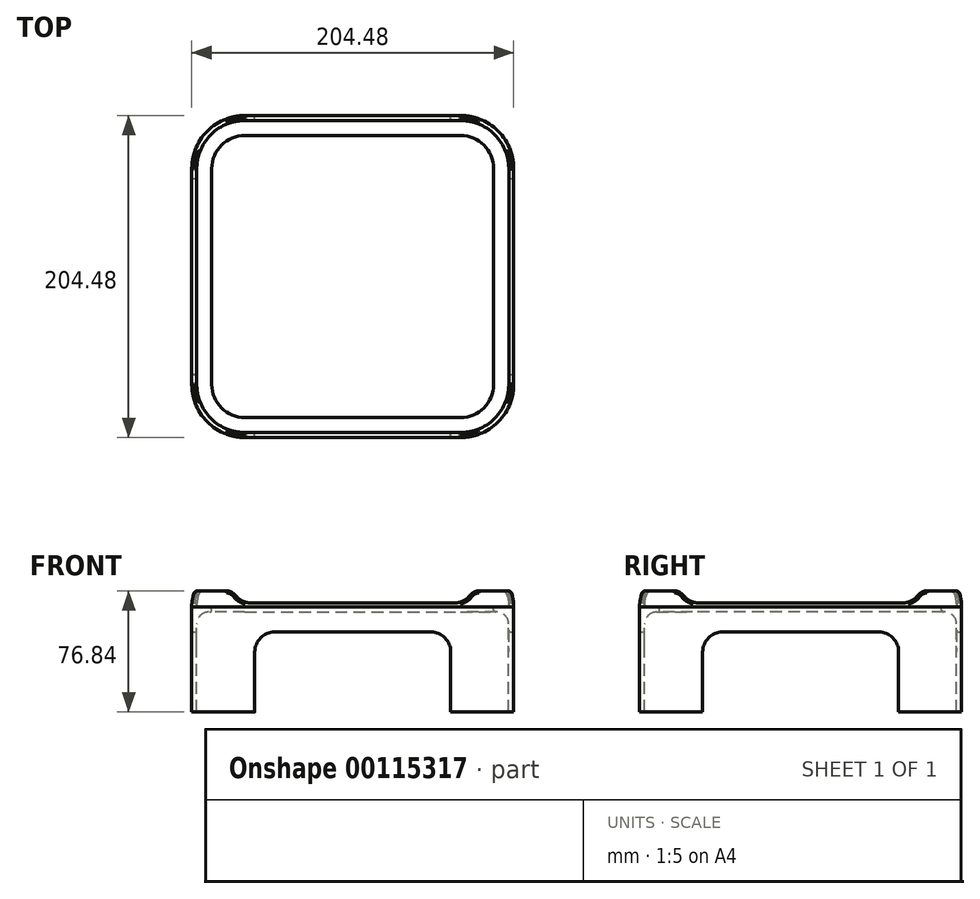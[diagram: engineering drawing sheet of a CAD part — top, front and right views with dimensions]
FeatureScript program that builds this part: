
annotation { "Feature Type Name" : "Feature", "Feature Type Description" : "" }
export const myFeature = defineFeature(function(context is Context, id is Id, definition is map)
    precondition{}
    {
        {
            var Q0;
            Q0=qCreatedBy(makeId("Top.planeOp"),FACE);
            var sketch = newSketch(context, id + "F0", { "sketchPlane" : qUnion([Q0])});
            skLineSegment(sketch, "E0.bottom", {"start": v(-99.06, 99.06) * mm, "end": v(99.06, 99.06) * mm});
            skLineSegment(sketch, "E0.top", {"start": v(-99.06, -99.06) * mm, "end": v(99.06, -99.06) * mm});
            skLineSegment(sketch, "E0.left", {"start": v(-99.06, 99.06) * mm, "end": v(-99.06, -99.06) * mm});
            skLineSegment(sketch, "E0.right", {"start": v(99.06, 99.06) * mm, "end": v(99.06, -99.06) * mm});
            skPoint(sketch, "E0.middle", {"position": v(0, 0) * mm});
            skSolve(sketch);
        }
        {
            var Q0;
            Q0=makeQuery(id+"F0.imprint","IMPRINT",FACE,{"disambiguationData":[TD([[makeQuery(id+"F0.imprint","IMPRINT",EDGE,{"derivedFrom":sQuery(id+"F0.wireOp",EDGE,"E0.bottom")}),-1.0]])]});
            extrude(context, id + "F1", {"entities" : qUnion([Q0]), "oppositeDirection" : true, "depth" : 63.5 * mm});
        }
        {
            var Q0;
            Q0=makeQuery(id+"F1.opExtrude","SWEPT_EDGE",EDGE,{"disambiguationData":[OSD([sQuery(id+"F0.wireOp",EDGE,"E0.top"),sQuery(id+"F0.wireOp",EDGE,"E0.right")])]});
            var Q1;
            Q1=makeQuery(id+"F1.opExtrude","SWEPT_EDGE",EDGE,{"disambiguationData":[OSD([sQuery(id+"F0.wireOp",EDGE,"E0.top"),sQuery(id+"F0.wireOp",EDGE,"E0.left")])]});
            var Q2;
            Q2=makeQuery(id+"F1.opExtrude","SWEPT_EDGE",EDGE,{"disambiguationData":[OSD([sQuery(id+"F0.wireOp",EDGE,"E0.bottom"),sQuery(id+"F0.wireOp",EDGE,"E0.right")])]});
            var Q3;
            Q3=makeQuery(id+"F1.opExtrude","SWEPT_EDGE",EDGE,{"disambiguationData":[OSD([sQuery(id+"F0.wireOp",EDGE,"E0.bottom"),sQuery(id+"F0.wireOp",EDGE,"E0.left")])]});
            fillet(context, id + "F2", {"entities" : qUnion([Q0, Q1, Q2, Q3]), "radius" : 30.48 * mm, "tangentPropagation" : true, "allowEdgeOverflow" : false});
        }
        {
            var Q0;
            Q0=makeQuery(id+"F1.opExtrude","CAP_FACE",FACE,{"disambiguationData":[OSD([sQuery(id+"F0.wireOp",EDGE,"E0.bottom"),sQuery(id+"F0.wireOp",EDGE,"E0.top"),sQuery(id+"F0.wireOp",EDGE,"E0.left"),sQuery(id+"F0.wireOp",EDGE,"E0.right")])],"isStart":false});
            shell(context, id + "F3", {"entities" : qUnion([Q0]), "thickness" : 3.17 * mm, "oppositeDirection" : true});
        }
        {
            var Q0;
            Q0=makeQuery(id+"F1.opExtrude","SWEPT_FACE",FACE,{"disambiguationData":[OSD([sQuery(id+"F0.wireOp",EDGE,"E0.bottom")])]});
            var sketch = newSketch(context, id + "F4", { "sketchPlane" : qUnion([Q0])});
            skLineSegment(sketch, "E1.bottom", {"start": v(-62.23, -12.7) * mm, "end": v(62.23, -12.7) * mm});
            skLineSegment(sketch, "E1.top", {"start": v(-62.23, -63.5) * mm, "end": v(62.23, -63.5) * mm});
            skLineSegment(sketch, "E1.left", {"start": v(-62.23, -12.7) * mm, "end": v(-62.23, -63.5) * mm});
            skLineSegment(sketch, "E1.right", {"start": v(62.23, -12.7) * mm, "end": v(62.23, -63.5) * mm});
            skSolve(sketch);
        }
        {
            var Q0;
            Q0=makeQuery(id+"F1.opExtrude","SWEPT_FACE",FACE,{"disambiguationData":[OSD([sQuery(id+"F0.wireOp",EDGE,"E0.right")])]});
            var sketch = newSketch(context, id + "F5", { "sketchPlane" : qUnion([Q0])});
            skLineSegment(sketch, "E2.bottom", {"start": v(-62.23, -12.7) * mm, "end": v(62.23, -12.7) * mm});
            skLineSegment(sketch, "E2.top", {"start": v(-62.23, -63.5) * mm, "end": v(62.23, -63.5) * mm});
            skLineSegment(sketch, "E2.left", {"start": v(-62.23, -12.7) * mm, "end": v(-62.23, -63.5) * mm});
            skLineSegment(sketch, "E2.right", {"start": v(62.23, -12.7) * mm, "end": v(62.23, -63.5) * mm});
            skSolve(sketch);
        }
        {
            var Q0;
            Q0=makeQuery(id+"F4.imprint","IMPRINT",FACE,{"disambiguationData":[TD([[makeQuery(id+"F4.imprint","IMPRINT",EDGE,{"derivedFrom":sQuery(id+"F4.wireOp",EDGE,"E1.bottom")}),-1.0]])]});
            extrude(context, id + "F6", {"entities" : qUnion([Q0]), "operationType" : NewBodyOperationType.REMOVE, "endBound" : BoundingType.THROUGH_ALL, "oppositeDirection" : true, "depth" : 25.4 * mm});
        }
        {
            var Q0;
            Q0=makeQuery(id+"F5.imprint","IMPRINT",FACE,{"disambiguationData":[TD([[makeQuery(id+"F5.imprint","IMPRINT",EDGE,{"derivedFrom":sQuery(id+"F5.wireOp",EDGE,"E2.bottom")}),-1.0]])]});
            extrude(context, id + "F7", {"entities" : qUnion([Q0]), "operationType" : NewBodyOperationType.REMOVE, "endBound" : BoundingType.THROUGH_ALL, "oppositeDirection" : true, "depth" : 25.4 * mm});
        }
        {
            var Q0;
            Q0=makeQuery(id+"F6.boolean.opBoolean","COPY",EDGE,{"disambiguationData":[OD(0.0)],"derivedFrom":makeQuery(id+"F6.opExtrude","SWEPT_EDGE",EDGE,{"disambiguationData":[OSD([sQuery(id+"F4.wireOp",EDGE,"E1.bottom"),sQuery(id+"F4.wireOp",EDGE,"E1.left")])]})});
            var Q1;
            Q1=makeQuery(id+"F6.boolean.opBoolean","COPY",EDGE,{"disambiguationData":[OD(0.0)],"derivedFrom":makeQuery(id+"F6.opExtrude","SWEPT_EDGE",EDGE,{"disambiguationData":[OSD([sQuery(id+"F4.wireOp",EDGE,"E1.bottom"),sQuery(id+"F4.wireOp",EDGE,"E1.right")])]})});
            var Q2;
            Q2=makeQuery(id+"F7.boolean.opBoolean","COPY",EDGE,{"disambiguationData":[OD(1.0)],"derivedFrom":makeQuery(id+"F7.opExtrude","SWEPT_EDGE",EDGE,{"disambiguationData":[OSD([sQuery(id+"F5.wireOp",EDGE,"E2.bottom"),sQuery(id+"F5.wireOp",EDGE,"E2.right")])]})});
            var Q3;
            Q3=makeQuery(id+"F7.boolean.opBoolean","COPY",EDGE,{"disambiguationData":[OD(1.0)],"derivedFrom":makeQuery(id+"F7.opExtrude","SWEPT_EDGE",EDGE,{"disambiguationData":[OSD([sQuery(id+"F5.wireOp",EDGE,"E2.bottom"),sQuery(id+"F5.wireOp",EDGE,"E2.left")])]})});
            var Q4;
            Q4=makeQuery(id+"F6.boolean.opBoolean","COPY",EDGE,{"disambiguationData":[OD(1.0)],"derivedFrom":makeQuery(id+"F6.opExtrude","SWEPT_EDGE",EDGE,{"disambiguationData":[OSD([sQuery(id+"F4.wireOp",EDGE,"E1.bottom"),sQuery(id+"F4.wireOp",EDGE,"E1.right")])]})});
            var Q5;
            Q5=makeQuery(id+"F7.boolean.opBoolean","COPY",EDGE,{"disambiguationData":[OD(0.0)],"derivedFrom":makeQuery(id+"F7.opExtrude","SWEPT_EDGE",EDGE,{"disambiguationData":[OSD([sQuery(id+"F5.wireOp",EDGE,"E2.bottom"),sQuery(id+"F5.wireOp",EDGE,"E2.right")])]})});
            var Q6;
            Q6=makeQuery(id+"F6.boolean.opBoolean","COPY",EDGE,{"disambiguationData":[OD(1.0)],"derivedFrom":makeQuery(id+"F6.opExtrude","SWEPT_EDGE",EDGE,{"disambiguationData":[OSD([sQuery(id+"F4.wireOp",EDGE,"E1.bottom"),sQuery(id+"F4.wireOp",EDGE,"E1.left")])]})});
            var Q7;
            Q7=makeQuery(id+"F7.boolean.opBoolean","COPY",EDGE,{"disambiguationData":[OD(0.0)],"derivedFrom":makeQuery(id+"F7.opExtrude","SWEPT_EDGE",EDGE,{"disambiguationData":[OSD([sQuery(id+"F5.wireOp",EDGE,"E2.bottom"),sQuery(id+"F5.wireOp",EDGE,"E2.left")])]})});
            fillet(context, id + "F8", {"entities" : qUnion([Q0, Q1, Q2, Q3, Q4, Q5, Q6, Q7]), "radius" : 12.7 * mm, "tangentPropagation" : true, "allowEdgeOverflow" : false});
        }
        {
            var Q0;
            Q0=makeQuery(id+"F1.opExtrude","CAP_FACE",FACE,{"disambiguationData":[OSD([sQuery(id+"F0.wireOp",EDGE,"E0.bottom"),sQuery(id+"F0.wireOp",EDGE,"E0.top"),sQuery(id+"F0.wireOp",EDGE,"E0.left"),sQuery(id+"F0.wireOp",EDGE,"E0.right")])],"isStart":true});
            extrude(context, id + "F9", {"entities" : qUnion([Q0]), "depth" : 10.16 * mm});
        }
        {
            var Q0;
            Q0=makeQuery(id+"F9.opExtrude","CAP_FACE",FACE,{"disambiguationData":[OSD([sQuery(id+"F0.wireOp",EDGE,"E0.bottom"),sQuery(id+"F0.wireOp",EDGE,"E0.top"),sQuery(id+"F0.wireOp",EDGE,"E0.left"),sQuery(id+"F0.wireOp",EDGE,"E0.right")])],"isStart":false});
            var Q1;
            Q1=makeQuery(id+"F9.opExtrude","CAP_FACE",FACE,{"disambiguationData":[OSD([sQuery(id+"F0.wireOp",EDGE,"E0.bottom"),sQuery(id+"F0.wireOp",EDGE,"E0.top"),sQuery(id+"F0.wireOp",EDGE,"E0.left"),sQuery(id+"F0.wireOp",EDGE,"E0.right")])],"isStart":true});
            shell(context, id + "F10", {"entities" : qUnion([Q0, Q1]), "thickness" : 3.15 * mm});
        }
        {
            var Q0;
            Q0=makeQuery(id+"F9.opExtrude","CAP_FACE",FACE,{"disambiguationData":[OSD([sQuery(id+"F0.wireOp",EDGE,"E0.bottom"),sQuery(id+"F0.wireOp",EDGE,"E0.top"),sQuery(id+"F0.wireOp",EDGE,"E0.left"),sQuery(id+"F0.wireOp",EDGE,"E0.right")])],"isStart":false});
            var sketch = newSketch(context, id + "F11", { "sketchPlane" : qUnion([Q0])});
            skLineSegment(sketch, "E3.bottom", {"start": v(-114.3, 76.2) * mm, "end": v(114.3, 76.2) * mm});
            skLineSegment(sketch, "E3.top", {"start": v(-114.3, -76.2) * mm, "end": v(114.3, -76.2) * mm});
            skLineSegment(sketch, "E3.left", {"start": v(-114.3, 76.2) * mm, "end": v(-114.3, -76.2) * mm});
            skLineSegment(sketch, "E3.right", {"start": v(114.3, 76.2) * mm, "end": v(114.3, -76.2) * mm});
            skPoint(sketch, "E3.middle", {"position": v(0, 0) * mm});
            skLineSegment(sketch, "E4.bottom", {"start": v(-76.2, 114.3) * mm, "end": v(76.2, 114.3) * mm});
            skLineSegment(sketch, "E4.top", {"start": v(-76.2, -114.3) * mm, "end": v(76.2, -114.3) * mm});
            skLineSegment(sketch, "E4.left", {"start": v(-76.2, 114.3) * mm, "end": v(-76.2, -114.3) * mm});
            skLineSegment(sketch, "E4.right", {"start": v(76.2, 114.3) * mm, "end": v(76.2, -114.3) * mm});
            skSolve(sketch);
        }
        {
            var Q0;
            {var subQ0=sQuery(id+"F11.wireOp",EDGE,"E3.right");Q0=makeQuery(id+"F11.imprint","IMPRINT",FACE,{"disambiguationData":[TD([[makeQuery(id+"F11.imprint","IMPRINT",EDGE,{"derivedFrom":subQ0}),-1.0]])]});}
            var Q1;
            {var subQ0=sQuery(id+"F11.wireOp",EDGE,"E4.right");var subQ1=sQuery(id+"F11.wireOp",EDGE,"E3.bottom");var subQ2=makeQuery(id+"F11.imprint","INTERSECT",VERTEX,{"derivedFrom":[subQ1,subQ0]});Q1=makeQuery(id+"F11.imprint","IMPRINT",FACE,{"disambiguationData":[TD([[makeQuery(id+"F11.imprint","IMPRINT",EDGE,{"disambiguationData":[TD([[subQ2,-1.0]])],"derivedFrom":subQ0}),1.0]])]});}
            var Q2;
            {var subQ0=sQuery(id+"F11.wireOp",EDGE,"E3.bottom");var subQ1=sQuery(id+"F0.wireOp",EDGE,"E0.right");var subQ2=makeQuery(id+"F9.opExtrude","CAP_EDGE",EDGE,{"disambiguationData":[OSD([subQ1])],"isStart":false});var subQ3=makeQuery(id+"F11.imprint","INTERSECT",VERTEX,{"derivedFrom":[subQ2,subQ0]});Q2=makeQuery(id+"F11.imprint","IMPRINT",FACE,{"disambiguationData":[TD([[makeQuery(id+"F11.imprint","IMPRINT",EDGE,{"disambiguationData":[TD([[subQ3,-1.0]])],"derivedFrom":subQ2}),-1.0]])]});}
            var Q3;
            {var subQ0=sQuery(id+"F11.wireOp",EDGE,"E4.left");var subQ1=sQuery(id+"F11.wireOp",EDGE,"E3.top");var subQ2=makeQuery(id+"F11.imprint","INTERSECT",VERTEX,{"derivedFrom":[subQ1,subQ0]});Q3=makeQuery(id+"F11.imprint","IMPRINT",FACE,{"disambiguationData":[TD([[makeQuery(id+"F11.imprint","IMPRINT",EDGE,{"disambiguationData":[TD([[subQ2,-1.0]])],"derivedFrom":subQ1}),-1.0]])]});}
            var Q4;
            {var subQ0=sQuery(id+"F11.wireOp",EDGE,"E4.left");var subQ1=sQuery(id+"F0.wireOp",EDGE,"E0.top");var subQ2=makeQuery(id+"F9.opExtrude","CAP_EDGE",EDGE,{"disambiguationData":[OSD([subQ1])],"isStart":false});var subQ3=makeQuery(id+"F11.imprint","INTERSECT",VERTEX,{"derivedFrom":[subQ2,subQ0]});Q4=makeQuery(id+"F11.imprint","IMPRINT",FACE,{"disambiguationData":[TD([[makeQuery(id+"F11.imprint","IMPRINT",EDGE,{"disambiguationData":[TD([[subQ3,-1.0]])],"derivedFrom":subQ2}),1.0]])]});}
            var Q5;
            {var subQ0=sQuery(id+"F11.wireOp",EDGE,"E4.top");Q5=makeQuery(id+"F11.imprint","IMPRINT",FACE,{"disambiguationData":[TD([[makeQuery(id+"F11.imprint","IMPRINT",EDGE,{"derivedFrom":subQ0}),1.0]])]});}
            var Q6;
            {var subQ0=sQuery(id+"F11.wireOp",EDGE,"E4.bottom");Q6=makeQuery(id+"F11.imprint","IMPRINT",FACE,{"disambiguationData":[TD([[makeQuery(id+"F11.imprint","IMPRINT",EDGE,{"derivedFrom":subQ0}),-1.0]])]});}
            var Q7;
            {var subQ0=sQuery(id+"F11.wireOp",EDGE,"E4.left");var subQ1=sQuery(id+"F11.wireOp",EDGE,"E3.bottom");var subQ2=makeQuery(id+"F11.imprint","INTERSECT",VERTEX,{"derivedFrom":[subQ1,subQ0]});Q7=makeQuery(id+"F11.imprint","IMPRINT",FACE,{"disambiguationData":[TD([[makeQuery(id+"F11.imprint","IMPRINT",EDGE,{"disambiguationData":[TD([[subQ2,-1.0]])],"derivedFrom":subQ1}),1.0]])]});}
            var Q8;
            {var subQ0=sQuery(id+"F11.wireOp",EDGE,"E4.left");var subQ1=sQuery(id+"F0.wireOp",EDGE,"E0.bottom");var subQ2=makeQuery(id+"F9.opExtrude","CAP_EDGE",EDGE,{"disambiguationData":[OSD([subQ1])],"isStart":false});var subQ3=makeQuery(id+"F11.imprint","INTERSECT",VERTEX,{"derivedFrom":[subQ2,subQ0]});Q8=makeQuery(id+"F11.imprint","IMPRINT",FACE,{"disambiguationData":[TD([[makeQuery(id+"F11.imprint","IMPRINT",EDGE,{"disambiguationData":[TD([[subQ3,-1.0]])],"derivedFrom":subQ2}),-1.0]])]});}
            var Q9;
            {var subQ0=sQuery(id+"F11.wireOp",EDGE,"E3.left");Q9=makeQuery(id+"F11.imprint","IMPRINT",FACE,{"disambiguationData":[TD([[makeQuery(id+"F11.imprint","IMPRINT",EDGE,{"derivedFrom":subQ0}),1.0]])]});}
            var Q10;
            {var subQ0=sQuery(id+"F11.wireOp",EDGE,"E3.bottom");var subQ1=sQuery(id+"F0.wireOp",EDGE,"E0.left");var subQ2=makeQuery(id+"F9.opExtrude","CAP_EDGE",EDGE,{"disambiguationData":[OSD([subQ1])],"isStart":false});var subQ3=makeQuery(id+"F11.imprint","INTERSECT",VERTEX,{"derivedFrom":[subQ2,subQ0]});Q10=makeQuery(id+"F11.imprint","IMPRINT",FACE,{"disambiguationData":[TD([[makeQuery(id+"F11.imprint","IMPRINT",EDGE,{"disambiguationData":[TD([[subQ3,-1.0]])],"derivedFrom":subQ2}),1.0]])]});}
            var Q11;
            {var subQ0=sQuery(id+"F11.wireOp",EDGE,"E4.left");var subQ1=sQuery(id+"F11.wireOp",EDGE,"E3.bottom");var subQ2=makeQuery(id+"F11.imprint","INTERSECT",VERTEX,{"derivedFrom":[subQ1,subQ0]});Q11=makeQuery(id+"F11.imprint","IMPRINT",FACE,{"disambiguationData":[TD([[makeQuery(id+"F11.imprint","IMPRINT",EDGE,{"disambiguationData":[TD([[subQ2,-1.0]])],"derivedFrom":subQ0}),-1.0]])]});}
            var Q12;
            {var subQ0=sQuery(id+"F11.wireOp",EDGE,"E4.left");var subQ1=sQuery(id+"F11.wireOp",EDGE,"E3.bottom");var subQ2=makeQuery(id+"F11.imprint","INTERSECT",VERTEX,{"derivedFrom":[subQ1,subQ0]});Q12=makeQuery(id+"F11.imprint","IMPRINT",FACE,{"disambiguationData":[TD([[makeQuery(id+"F11.imprint","IMPRINT",EDGE,{"disambiguationData":[TD([[subQ2,-1.0]])],"derivedFrom":subQ1}),-1.0]])]});}
            extrude(context, id + "F12", {"entities" : qUnion([Q0, Q1, Q2, Q3, Q4, Q5, Q6, Q7, Q8, Q9, Q10, Q11, Q12]), "operationType" : NewBodyOperationType.REMOVE, "oppositeDirection" : true, "depth" : 7.62 * mm});
        }
        {
            var Q0;
            {var subQ0=sQuery(id+"F11.wireOp",EDGE,"E3.bottom");var subQ1=sQuery(id+"F0.wireOp",EDGE,"E0.left");var subQ2=makeQuery(id+"F9.opExtrude","CAP_EDGE",EDGE,{"disambiguationData":[OSD([subQ1])],"isStart":false});var subQ4=makeQuery(id+"F11.imprint","INTERSECT",VERTEX,{"derivedFrom":[subQ2,subQ0]});Q0=makeQuery(id+"F12.boolean.opBoolean","COPY",EDGE,{"derivedFrom":makeQuery(id+"F12.opExtrude","CAP_EDGE",EDGE,{"disambiguationData":[OSD([subQ0]),TDD([makeQuery(id+"F11.imprint","IMPRINT",EDGE,{"disambiguationData":[TD([[makeQuery(id+"F11.imprint","INTERSECT",VERTEX,{"derivedFrom":[subQ0,sQuery(id+"F11.wireOp",EDGE,"E3.left")]}),-1.0]])],"derivedFrom":subQ0}),makeQuery(id+"F11.imprint","IMPRINT",EDGE,{"disambiguationData":[TD([[subQ4,-1.0]])],"derivedFrom":subQ0}),makeQuery(id+"F11.imprint","IMPRINT",EDGE,{"disambiguationData":[TD([[makeQuery(id+"F11.imprint","INTERSECT",VERTEX,{"derivedFrom":[subQ0,sQuery(id+"F11.wireOp",EDGE,"E4.left")]}),1.0]])],"derivedFrom":subQ0})])],"isStart":false})});}
            var Q1;
            {var subQ0=sQuery(id+"F11.wireOp",EDGE,"E3.top");var subQ1=sQuery(id+"F0.wireOp",EDGE,"E0.left");var subQ2=makeQuery(id+"F9.opExtrude","CAP_EDGE",EDGE,{"disambiguationData":[OSD([subQ1])],"isStart":false});var subQ4=makeQuery(id+"F11.imprint","INTERSECT",VERTEX,{"derivedFrom":[subQ2,subQ0]});Q1=makeQuery(id+"F12.boolean.opBoolean","COPY",EDGE,{"derivedFrom":makeQuery(id+"F12.opExtrude","CAP_EDGE",EDGE,{"disambiguationData":[OSD([subQ0]),TDD([makeQuery(id+"F11.imprint","IMPRINT",EDGE,{"disambiguationData":[TD([[makeQuery(id+"F11.imprint","INTERSECT",VERTEX,{"derivedFrom":[subQ0,sQuery(id+"F11.wireOp",EDGE,"E3.left")]}),-1.0]])],"derivedFrom":subQ0}),makeQuery(id+"F11.imprint","IMPRINT",EDGE,{"disambiguationData":[TD([[subQ4,-1.0]])],"derivedFrom":subQ0}),makeQuery(id+"F11.imprint","IMPRINT",EDGE,{"disambiguationData":[TD([[makeQuery(id+"F11.imprint","INTERSECT",VERTEX,{"derivedFrom":[subQ0,sQuery(id+"F11.wireOp",EDGE,"E4.left")]}),1.0]])],"derivedFrom":subQ0})])],"isStart":false})});}
            var Q2;
            {var subQ0=sQuery(id+"F11.wireOp",EDGE,"E4.left");var subQ1=sQuery(id+"F0.wireOp",EDGE,"E0.top");var subQ2=makeQuery(id+"F9.opExtrude","CAP_EDGE",EDGE,{"disambiguationData":[OSD([subQ1])],"isStart":false});var subQ3=makeQuery(id+"F11.imprint","INTERSECT",VERTEX,{"derivedFrom":[subQ2,subQ0]});Q2=makeQuery(id+"F12.boolean.opBoolean","COPY",EDGE,{"derivedFrom":makeQuery(id+"F12.opExtrude","CAP_EDGE",EDGE,{"disambiguationData":[OSD([subQ0]),TDD([makeQuery(id+"F11.imprint","IMPRINT",EDGE,{"disambiguationData":[TD([[makeQuery(id+"F11.imprint","INTERSECT",VERTEX,{"derivedFrom":[sQuery(id+"F11.wireOp",EDGE,"E3.top"),subQ0]}),-1.0]])],"derivedFrom":subQ0}),makeQuery(id+"F11.imprint","IMPRINT",EDGE,{"disambiguationData":[TD([[subQ3,1.0]])],"derivedFrom":subQ0}),makeQuery(id+"F11.imprint","IMPRINT",EDGE,{"disambiguationData":[TD([[makeQuery(id+"F11.imprint","INTERSECT",VERTEX,{"derivedFrom":[sQuery(id+"F11.wireOp",EDGE,"E4.top"),subQ0]}),1.0]])],"derivedFrom":subQ0})])],"isStart":false})});}
            var Q3;
            {var subQ0=sQuery(id+"F11.wireOp",EDGE,"E4.right");var subQ1=sQuery(id+"F0.wireOp",EDGE,"E0.top");var subQ2=makeQuery(id+"F9.opExtrude","CAP_EDGE",EDGE,{"disambiguationData":[OSD([subQ1])],"isStart":false});var subQ3=makeQuery(id+"F11.imprint","INTERSECT",VERTEX,{"derivedFrom":[subQ2,subQ0]});Q3=makeQuery(id+"F12.boolean.opBoolean","COPY",EDGE,{"derivedFrom":makeQuery(id+"F12.opExtrude","CAP_EDGE",EDGE,{"disambiguationData":[OSD([subQ0]),TDD([makeQuery(id+"F11.imprint","IMPRINT",EDGE,{"disambiguationData":[TD([[makeQuery(id+"F11.imprint","INTERSECT",VERTEX,{"derivedFrom":[sQuery(id+"F11.wireOp",EDGE,"E3.top"),subQ0]}),-1.0]])],"derivedFrom":subQ0}),makeQuery(id+"F11.imprint","IMPRINT",EDGE,{"disambiguationData":[TD([[subQ3,1.0]])],"derivedFrom":subQ0}),makeQuery(id+"F11.imprint","IMPRINT",EDGE,{"disambiguationData":[TD([[makeQuery(id+"F11.imprint","INTERSECT",VERTEX,{"derivedFrom":[sQuery(id+"F11.wireOp",EDGE,"E4.top"),subQ0]}),1.0]])],"derivedFrom":subQ0})])],"isStart":false})});}
            var Q4;
            {var subQ0=sQuery(id+"F11.wireOp",EDGE,"E3.top");var subQ1=sQuery(id+"F0.wireOp",EDGE,"E0.right");var subQ2=makeQuery(id+"F9.opExtrude","CAP_EDGE",EDGE,{"disambiguationData":[OSD([subQ1])],"isStart":false});var subQ3=makeQuery(id+"F11.imprint","INTERSECT",VERTEX,{"derivedFrom":[subQ2,subQ0]});Q4=makeQuery(id+"F12.boolean.opBoolean","COPY",EDGE,{"derivedFrom":makeQuery(id+"F12.opExtrude","CAP_EDGE",EDGE,{"disambiguationData":[OSD([subQ0]),TDD([makeQuery(id+"F11.imprint","IMPRINT",EDGE,{"disambiguationData":[TD([[makeQuery(id+"F11.imprint","INTERSECT",VERTEX,{"derivedFrom":[subQ0,sQuery(id+"F11.wireOp",EDGE,"E4.right")]}),-1.0]])],"derivedFrom":subQ0}),makeQuery(id+"F11.imprint","IMPRINT",EDGE,{"disambiguationData":[TD([[subQ3,1.0]])],"derivedFrom":subQ0}),makeQuery(id+"F11.imprint","IMPRINT",EDGE,{"disambiguationData":[TD([[makeQuery(id+"F11.imprint","INTERSECT",VERTEX,{"derivedFrom":[subQ0,sQuery(id+"F11.wireOp",EDGE,"E3.right")]}),1.0]])],"derivedFrom":subQ0})])],"isStart":false})});}
            var Q5;
            {var subQ0=sQuery(id+"F11.wireOp",EDGE,"E3.bottom");var subQ1=sQuery(id+"F0.wireOp",EDGE,"E0.right");var subQ2=makeQuery(id+"F9.opExtrude","CAP_EDGE",EDGE,{"disambiguationData":[OSD([subQ1])],"isStart":false});var subQ3=makeQuery(id+"F11.imprint","INTERSECT",VERTEX,{"derivedFrom":[subQ2,subQ0]});Q5=makeQuery(id+"F12.boolean.opBoolean","COPY",EDGE,{"derivedFrom":makeQuery(id+"F12.opExtrude","CAP_EDGE",EDGE,{"disambiguationData":[OSD([subQ0]),TDD([makeQuery(id+"F11.imprint","IMPRINT",EDGE,{"disambiguationData":[TD([[makeQuery(id+"F11.imprint","INTERSECT",VERTEX,{"derivedFrom":[subQ0,sQuery(id+"F11.wireOp",EDGE,"E4.right")]}),-1.0]])],"derivedFrom":subQ0}),makeQuery(id+"F11.imprint","IMPRINT",EDGE,{"disambiguationData":[TD([[subQ3,1.0]])],"derivedFrom":subQ0}),makeQuery(id+"F11.imprint","IMPRINT",EDGE,{"disambiguationData":[TD([[makeQuery(id+"F11.imprint","INTERSECT",VERTEX,{"derivedFrom":[subQ0,sQuery(id+"F11.wireOp",EDGE,"E3.right")]}),1.0]])],"derivedFrom":subQ0})])],"isStart":false})});}
            var Q6;
            {var subQ0=sQuery(id+"F11.wireOp",EDGE,"E4.right");var subQ1=sQuery(id+"F0.wireOp",EDGE,"E0.bottom");var subQ2=makeQuery(id+"F9.opExtrude","CAP_EDGE",EDGE,{"disambiguationData":[OSD([subQ1])],"isStart":false});var subQ4=makeQuery(id+"F11.imprint","INTERSECT",VERTEX,{"derivedFrom":[subQ2,subQ0]});Q6=makeQuery(id+"F12.boolean.opBoolean","COPY",EDGE,{"derivedFrom":makeQuery(id+"F12.opExtrude","CAP_EDGE",EDGE,{"disambiguationData":[OSD([subQ0]),TDD([makeQuery(id+"F11.imprint","IMPRINT",EDGE,{"disambiguationData":[TD([[makeQuery(id+"F11.imprint","INTERSECT",VERTEX,{"derivedFrom":[sQuery(id+"F11.wireOp",EDGE,"E4.bottom"),subQ0]}),-1.0]])],"derivedFrom":subQ0}),makeQuery(id+"F11.imprint","IMPRINT",EDGE,{"disambiguationData":[TD([[subQ4,-1.0]])],"derivedFrom":subQ0}),makeQuery(id+"F11.imprint","IMPRINT",EDGE,{"disambiguationData":[TD([[makeQuery(id+"F11.imprint","INTERSECT",VERTEX,{"derivedFrom":[sQuery(id+"F11.wireOp",EDGE,"E3.bottom"),subQ0]}),1.0]])],"derivedFrom":subQ0})])],"isStart":false})});}
            var Q7;
            {var subQ0=sQuery(id+"F11.wireOp",EDGE,"E4.left");var subQ1=sQuery(id+"F0.wireOp",EDGE,"E0.bottom");var subQ2=makeQuery(id+"F9.opExtrude","CAP_EDGE",EDGE,{"disambiguationData":[OSD([subQ1])],"isStart":false});var subQ4=makeQuery(id+"F11.imprint","INTERSECT",VERTEX,{"derivedFrom":[subQ2,subQ0]});Q7=makeQuery(id+"F12.boolean.opBoolean","COPY",EDGE,{"derivedFrom":makeQuery(id+"F12.opExtrude","CAP_EDGE",EDGE,{"disambiguationData":[OSD([subQ0]),TDD([makeQuery(id+"F11.imprint","IMPRINT",EDGE,{"disambiguationData":[TD([[makeQuery(id+"F11.imprint","INTERSECT",VERTEX,{"derivedFrom":[sQuery(id+"F11.wireOp",EDGE,"E4.bottom"),subQ0]}),-1.0]])],"derivedFrom":subQ0}),makeQuery(id+"F11.imprint","IMPRINT",EDGE,{"disambiguationData":[TD([[subQ4,-1.0]])],"derivedFrom":subQ0}),makeQuery(id+"F11.imprint","IMPRINT",EDGE,{"disambiguationData":[TD([[makeQuery(id+"F11.imprint","INTERSECT",VERTEX,{"derivedFrom":[sQuery(id+"F11.wireOp",EDGE,"E3.bottom"),subQ0]}),1.0]])],"derivedFrom":subQ0})])],"isStart":false})});}
            fillet(context, id + "F13", {"entities" : qUnion([Q0, Q1, Q2, Q3, Q4, Q5, Q6, Q7]), "radius" : 12.7 * mm, "tangentPropagation" : true, "allowEdgeOverflow" : false});
        }
        {
            var Q0;
            {var subQ0=sQuery(id+"F0.wireOp",EDGE,"E0.right");var subQ1=sQuery(id+"F0.wireOp",EDGE,"E0.left");var subQ2=sQuery(id+"F0.wireOp",EDGE,"E0.top");var subQ3=sQuery(id+"F0.wireOp",EDGE,"E0.bottom");var subQ5=sQuery(id+"F11.wireOp",EDGE,"E4.right");var subQ6=makeQuery(id+"F9.opExtrude","CAP_EDGE",EDGE,{"disambiguationData":[OSD([subQ2])],"isStart":false});var subQ7=makeQuery(id+"F11.imprint","INTERSECT",VERTEX,{"derivedFrom":[subQ6,subQ5]});var subQ8=makeQuery(id+"F11.imprint","IMPRINT",EDGE,{"disambiguationData":[TD([[makeQuery(id+"F11.imprint","INTERSECT",VERTEX,{"derivedFrom":[sQuery(id+"F11.wireOp",EDGE,"E4.top"),subQ5]}),1.0]])],"derivedFrom":subQ5});var subQ10=makeQuery(id+"F11.imprint","IMPRINT",EDGE,{"disambiguationData":[TD([[subQ7,1.0]])],"derivedFrom":subQ5});var subQ11=sQuery(id+"F11.wireOp",EDGE,"E3.top");var subQ12=makeQuery(id+"F11.imprint","INTERSECT",VERTEX,{"derivedFrom":[subQ11,subQ5]});var subQ13=makeQuery(id+"F11.imprint","IMPRINT",EDGE,{"disambiguationData":[TD([[subQ12,-1.0]])],"derivedFrom":subQ5});var subQ14=makeQuery(id+"F9.opExtrude","CAP_EDGE",EDGE,{"disambiguationData":[OSD([subQ0])],"isStart":false});var subQ15=makeQuery(id+"F11.imprint","INTERSECT",VERTEX,{"derivedFrom":[subQ14,subQ11]});Q0=makeQuery(id+"F13.opFillet","BLEND_EDGE",EDGE,{"blendedFrom":[makeQuery(id+"F12.boolean.opBoolean","COPY",EDGE,{"derivedFrom":makeQuery(id+"F12.opExtrude","CAP_EDGE",EDGE,{"disambiguationData":[OSD([subQ5]),TDD([subQ13,subQ10,subQ8])],"isStart":false})}),makeQuery(id+"F12.boolean.opBoolean","SPLIT",FACE,{"disambiguationData":[TD([makeQuery(id+"F12.opExtrude","SWEPT_FACE",FACE,{"disambiguationData":[OSD([subQ11]),TDD([makeQuery(id+"F11.imprint","IMPRINT",EDGE,{"disambiguationData":[TD([[subQ12,-1.0]])],"derivedFrom":subQ11}),makeQuery(id+"F11.imprint","IMPRINT",EDGE,{"disambiguationData":[TD([[subQ15,1.0]])],"derivedFrom":subQ11}),makeQuery(id+"F11.imprint","IMPRINT",EDGE,{"disambiguationData":[TD([[makeQuery(id+"F11.imprint","INTERSECT",VERTEX,{"derivedFrom":[subQ11,sQuery(id+"F11.wireOp",EDGE,"E3.right")]}),1.0]])],"derivedFrom":subQ11})])]})])],"derivedFrom":makeQuery(id+"F9.opExtrude","CAP_FACE",FACE,{"disambiguationData":[OSD([subQ3,subQ2,subQ1,subQ0])],"isStart":false})})],"blendedInto":[makeQuery(id+"F12.boolean.opBoolean","SPLIT",FACE,{"disambiguationData":[TD([makeQuery(id+"F12.opExtrude","SWEPT_FACE",FACE,{"disambiguationData":[OSD([subQ11]),TDD([makeQuery(id+"F11.imprint","IMPRINT",EDGE,{"disambiguationData":[TD([[subQ12,-1.0]])],"derivedFrom":subQ11}),makeQuery(id+"F11.imprint","IMPRINT",EDGE,{"disambiguationData":[TD([[subQ15,1.0]])],"derivedFrom":subQ11}),makeQuery(id+"F11.imprint","IMPRINT",EDGE,{"disambiguationData":[TD([[makeQuery(id+"F11.imprint","INTERSECT",VERTEX,{"derivedFrom":[subQ11,sQuery(id+"F11.wireOp",EDGE,"E3.right")]}),1.0]])],"derivedFrom":subQ11})])]})])],"derivedFrom":makeQuery(id+"F9.opExtrude","CAP_FACE",FACE,{"disambiguationData":[OSD([subQ3,subQ2,subQ1,subQ0])],"isStart":false})})]});}
            var Q1;
            {var subQ0=sQuery(id+"F0.wireOp",EDGE,"E0.right");var subQ1=sQuery(id+"F0.wireOp",EDGE,"E0.left");var subQ2=sQuery(id+"F0.wireOp",EDGE,"E0.top");var subQ3=sQuery(id+"F0.wireOp",EDGE,"E0.bottom");var subQ5=sQuery(id+"F11.wireOp",EDGE,"E4.right");var subQ9=sQuery(id+"F11.wireOp",EDGE,"E3.top");var subQ10=makeQuery(id+"F11.imprint","INTERSECT",VERTEX,{"derivedFrom":[subQ9,subQ5]});var subQ11=makeQuery(id+"F9.opExtrude","CAP_EDGE",EDGE,{"disambiguationData":[OSD([subQ0])],"isStart":false});var subQ12=makeQuery(id+"F11.imprint","INTERSECT",VERTEX,{"derivedFrom":[subQ11,subQ9]});var subQ13=makeQuery(id+"F11.imprint","IMPRINT",EDGE,{"disambiguationData":[TD([[makeQuery(id+"F11.imprint","INTERSECT",VERTEX,{"derivedFrom":[subQ9,sQuery(id+"F11.wireOp",EDGE,"E3.right")]}),1.0]])],"derivedFrom":subQ9});var subQ15=makeQuery(id+"F11.imprint","IMPRINT",EDGE,{"disambiguationData":[TD([[subQ12,1.0]])],"derivedFrom":subQ9});var subQ16=makeQuery(id+"F11.imprint","IMPRINT",EDGE,{"disambiguationData":[TD([[subQ10,-1.0]])],"derivedFrom":subQ9});Q1=makeQuery(id+"F13.opFillet","BLEND_EDGE",EDGE,{"blendedFrom":[makeQuery(id+"F12.boolean.opBoolean","COPY",EDGE,{"derivedFrom":makeQuery(id+"F12.opExtrude","CAP_EDGE",EDGE,{"disambiguationData":[OSD([subQ9]),TDD([subQ16,subQ15,subQ13])],"isStart":false})}),makeQuery(id+"F12.boolean.opBoolean","SPLIT",FACE,{"disambiguationData":[TD([makeQuery(id+"F12.opExtrude","SWEPT_FACE",FACE,{"disambiguationData":[OSD([subQ9]),TDD([subQ16,subQ15,subQ13])]})])],"derivedFrom":makeQuery(id+"F9.opExtrude","CAP_FACE",FACE,{"disambiguationData":[OSD([subQ3,subQ2,subQ1,subQ0])],"isStart":false})})],"blendedInto":[makeQuery(id+"F12.boolean.opBoolean","SPLIT",FACE,{"disambiguationData":[TD([makeQuery(id+"F12.opExtrude","SWEPT_FACE",FACE,{"disambiguationData":[OSD([subQ9]),TDD([subQ16,subQ15,subQ13])]})])],"derivedFrom":makeQuery(id+"F9.opExtrude","CAP_FACE",FACE,{"disambiguationData":[OSD([subQ3,subQ2,subQ1,subQ0])],"isStart":false})})]});}
            var Q2;
            {var subQ0=sQuery(id+"F0.wireOp",EDGE,"E0.right");var subQ1=sQuery(id+"F0.wireOp",EDGE,"E0.left");var subQ2=sQuery(id+"F0.wireOp",EDGE,"E0.top");var subQ3=sQuery(id+"F0.wireOp",EDGE,"E0.bottom");var subQ5=sQuery(id+"F11.wireOp",EDGE,"E4.left");var subQ6=makeQuery(id+"F9.opExtrude","CAP_EDGE",EDGE,{"disambiguationData":[OSD([subQ2])],"isStart":false});var subQ7=makeQuery(id+"F11.imprint","INTERSECT",VERTEX,{"derivedFrom":[subQ6,subQ5]});var subQ8=makeQuery(id+"F11.imprint","IMPRINT",EDGE,{"disambiguationData":[TD([[makeQuery(id+"F11.imprint","INTERSECT",VERTEX,{"derivedFrom":[sQuery(id+"F11.wireOp",EDGE,"E4.top"),subQ5]}),1.0]])],"derivedFrom":subQ5});var subQ10=makeQuery(id+"F11.imprint","IMPRINT",EDGE,{"disambiguationData":[TD([[subQ7,1.0]])],"derivedFrom":subQ5});var subQ11=sQuery(id+"F11.wireOp",EDGE,"E3.top");var subQ12=makeQuery(id+"F11.imprint","INTERSECT",VERTEX,{"derivedFrom":[subQ11,subQ5]});var subQ13=makeQuery(id+"F11.imprint","IMPRINT",EDGE,{"disambiguationData":[TD([[subQ12,-1.0]])],"derivedFrom":subQ5});var subQ14=makeQuery(id+"F9.opExtrude","CAP_EDGE",EDGE,{"disambiguationData":[OSD([subQ1])],"isStart":false});var subQ16=makeQuery(id+"F11.imprint","INTERSECT",VERTEX,{"derivedFrom":[subQ14,subQ11]});Q2=makeQuery(id+"F13.opFillet","BLEND_EDGE",EDGE,{"blendedFrom":[makeQuery(id+"F12.boolean.opBoolean","COPY",EDGE,{"derivedFrom":makeQuery(id+"F12.opExtrude","CAP_EDGE",EDGE,{"disambiguationData":[OSD([subQ5]),TDD([subQ13,subQ10,subQ8])],"isStart":false})}),makeQuery(id+"F12.boolean.opBoolean","SPLIT",FACE,{"disambiguationData":[TD([makeQuery(id+"F12.opExtrude","SWEPT_FACE",FACE,{"disambiguationData":[OSD([subQ11]),TDD([makeQuery(id+"F11.imprint","IMPRINT",EDGE,{"disambiguationData":[TD([[makeQuery(id+"F11.imprint","INTERSECT",VERTEX,{"derivedFrom":[subQ11,sQuery(id+"F11.wireOp",EDGE,"E3.left")]}),-1.0]])],"derivedFrom":subQ11}),makeQuery(id+"F11.imprint","IMPRINT",EDGE,{"disambiguationData":[TD([[subQ16,-1.0]])],"derivedFrom":subQ11}),makeQuery(id+"F11.imprint","IMPRINT",EDGE,{"disambiguationData":[TD([[subQ12,1.0]])],"derivedFrom":subQ11})])]})])],"derivedFrom":makeQuery(id+"F9.opExtrude","CAP_FACE",FACE,{"disambiguationData":[OSD([subQ3,subQ2,subQ1,subQ0])],"isStart":false})})],"blendedInto":[makeQuery(id+"F12.boolean.opBoolean","SPLIT",FACE,{"disambiguationData":[TD([makeQuery(id+"F12.opExtrude","SWEPT_FACE",FACE,{"disambiguationData":[OSD([subQ11]),TDD([makeQuery(id+"F11.imprint","IMPRINT",EDGE,{"disambiguationData":[TD([[makeQuery(id+"F11.imprint","INTERSECT",VERTEX,{"derivedFrom":[subQ11,sQuery(id+"F11.wireOp",EDGE,"E3.left")]}),-1.0]])],"derivedFrom":subQ11}),makeQuery(id+"F11.imprint","IMPRINT",EDGE,{"disambiguationData":[TD([[subQ16,-1.0]])],"derivedFrom":subQ11}),makeQuery(id+"F11.imprint","IMPRINT",EDGE,{"disambiguationData":[TD([[subQ12,1.0]])],"derivedFrom":subQ11})])]})])],"derivedFrom":makeQuery(id+"F9.opExtrude","CAP_FACE",FACE,{"disambiguationData":[OSD([subQ3,subQ2,subQ1,subQ0])],"isStart":false})})]});}
            var Q3;
            {var subQ0=sQuery(id+"F0.wireOp",EDGE,"E0.right");var subQ1=sQuery(id+"F0.wireOp",EDGE,"E0.left");var subQ2=sQuery(id+"F0.wireOp",EDGE,"E0.top");var subQ3=sQuery(id+"F0.wireOp",EDGE,"E0.bottom");var subQ5=sQuery(id+"F11.wireOp",EDGE,"E4.left");var subQ9=sQuery(id+"F11.wireOp",EDGE,"E3.top");var subQ10=makeQuery(id+"F11.imprint","INTERSECT",VERTEX,{"derivedFrom":[subQ9,subQ5]});var subQ11=makeQuery(id+"F9.opExtrude","CAP_EDGE",EDGE,{"disambiguationData":[OSD([subQ1])],"isStart":false});var subQ13=makeQuery(id+"F11.imprint","IMPRINT",EDGE,{"disambiguationData":[TD([[subQ10,1.0]])],"derivedFrom":subQ9});var subQ14=makeQuery(id+"F11.imprint","INTERSECT",VERTEX,{"derivedFrom":[subQ11,subQ9]});var subQ15=makeQuery(id+"F11.imprint","IMPRINT",EDGE,{"disambiguationData":[TD([[subQ14,-1.0]])],"derivedFrom":subQ9});var subQ16=makeQuery(id+"F11.imprint","IMPRINT",EDGE,{"disambiguationData":[TD([[makeQuery(id+"F11.imprint","INTERSECT",VERTEX,{"derivedFrom":[subQ9,sQuery(id+"F11.wireOp",EDGE,"E3.left")]}),-1.0]])],"derivedFrom":subQ9});Q3=makeQuery(id+"F13.opFillet","BLEND_EDGE",EDGE,{"blendedFrom":[makeQuery(id+"F12.boolean.opBoolean","COPY",EDGE,{"derivedFrom":makeQuery(id+"F12.opExtrude","CAP_EDGE",EDGE,{"disambiguationData":[OSD([subQ9]),TDD([subQ16,subQ15,subQ13])],"isStart":false})}),makeQuery(id+"F12.boolean.opBoolean","SPLIT",FACE,{"disambiguationData":[TD([makeQuery(id+"F12.opExtrude","SWEPT_FACE",FACE,{"disambiguationData":[OSD([subQ9]),TDD([subQ16,subQ15,subQ13])]})])],"derivedFrom":makeQuery(id+"F9.opExtrude","CAP_FACE",FACE,{"disambiguationData":[OSD([subQ3,subQ2,subQ1,subQ0])],"isStart":false})})],"blendedInto":[makeQuery(id+"F12.boolean.opBoolean","SPLIT",FACE,{"disambiguationData":[TD([makeQuery(id+"F12.opExtrude","SWEPT_FACE",FACE,{"disambiguationData":[OSD([subQ9]),TDD([subQ16,subQ15,subQ13])]})])],"derivedFrom":makeQuery(id+"F9.opExtrude","CAP_FACE",FACE,{"disambiguationData":[OSD([subQ3,subQ2,subQ1,subQ0])],"isStart":false})})]});}
            var Q4;
            {var subQ0=sQuery(id+"F0.wireOp",EDGE,"E0.right");var subQ1=sQuery(id+"F0.wireOp",EDGE,"E0.bottom");var subQ2=sQuery(id+"F0.wireOp",EDGE,"E0.left");var subQ3=sQuery(id+"F0.wireOp",EDGE,"E0.top");var subQ5=sQuery(id+"F11.wireOp",EDGE,"E3.bottom");var subQ6=makeQuery(id+"F9.opExtrude","CAP_EDGE",EDGE,{"disambiguationData":[OSD([subQ0])],"isStart":false});var subQ7=makeQuery(id+"F11.imprint","INTERSECT",VERTEX,{"derivedFrom":[subQ6,subQ5]});var subQ8=makeQuery(id+"F11.imprint","IMPRINT",EDGE,{"disambiguationData":[TD([[makeQuery(id+"F11.imprint","INTERSECT",VERTEX,{"derivedFrom":[subQ5,sQuery(id+"F11.wireOp",EDGE,"E3.right")]}),1.0]])],"derivedFrom":subQ5});var subQ10=makeQuery(id+"F11.imprint","IMPRINT",EDGE,{"disambiguationData":[TD([[subQ7,1.0]])],"derivedFrom":subQ5});var subQ11=sQuery(id+"F11.wireOp",EDGE,"E4.right");var subQ12=makeQuery(id+"F11.imprint","INTERSECT",VERTEX,{"derivedFrom":[subQ5,subQ11]});var subQ13=makeQuery(id+"F11.imprint","IMPRINT",EDGE,{"disambiguationData":[TD([[subQ12,-1.0]])],"derivedFrom":subQ5});Q4=makeQuery(id+"F13.opFillet","BLEND_EDGE",EDGE,{"blendedFrom":[makeQuery(id+"F12.boolean.opBoolean","COPY",EDGE,{"derivedFrom":makeQuery(id+"F12.opExtrude","CAP_EDGE",EDGE,{"disambiguationData":[OSD([subQ5]),TDD([subQ13,subQ10,subQ8])],"isStart":false})}),makeQuery(id+"F12.boolean.opBoolean","SPLIT",FACE,{"disambiguationData":[TD([makeQuery(id+"F12.opExtrude","SWEPT_FACE",FACE,{"disambiguationData":[OSD([subQ5]),TDD([subQ13,subQ10,subQ8])]})])],"derivedFrom":makeQuery(id+"F9.opExtrude","CAP_FACE",FACE,{"disambiguationData":[OSD([subQ1,subQ3,subQ2,subQ0])],"isStart":false})})],"blendedInto":[makeQuery(id+"F12.boolean.opBoolean","SPLIT",FACE,{"disambiguationData":[TD([makeQuery(id+"F12.opExtrude","SWEPT_FACE",FACE,{"disambiguationData":[OSD([subQ5]),TDD([subQ13,subQ10,subQ8])]})])],"derivedFrom":makeQuery(id+"F9.opExtrude","CAP_FACE",FACE,{"disambiguationData":[OSD([subQ1,subQ3,subQ2,subQ0])],"isStart":false})})]});}
            var Q5;
            {var subQ0=sQuery(id+"F0.wireOp",EDGE,"E0.right");var subQ1=sQuery(id+"F0.wireOp",EDGE,"E0.bottom");var subQ2=sQuery(id+"F0.wireOp",EDGE,"E0.left");var subQ3=sQuery(id+"F0.wireOp",EDGE,"E0.top");var subQ5=sQuery(id+"F11.wireOp",EDGE,"E3.bottom");var subQ6=makeQuery(id+"F9.opExtrude","CAP_EDGE",EDGE,{"disambiguationData":[OSD([subQ0])],"isStart":false});var subQ7=makeQuery(id+"F11.imprint","INTERSECT",VERTEX,{"derivedFrom":[subQ6,subQ5]});var subQ9=sQuery(id+"F11.wireOp",EDGE,"E4.right");var subQ10=makeQuery(id+"F11.imprint","INTERSECT",VERTEX,{"derivedFrom":[subQ5,subQ9]});var subQ11=makeQuery(id+"F9.opExtrude","CAP_EDGE",EDGE,{"disambiguationData":[OSD([subQ1])],"isStart":false});var subQ13=makeQuery(id+"F11.imprint","IMPRINT",EDGE,{"disambiguationData":[TD([[subQ10,1.0]])],"derivedFrom":subQ9});var subQ14=makeQuery(id+"F11.imprint","INTERSECT",VERTEX,{"derivedFrom":[subQ11,subQ9]});var subQ15=makeQuery(id+"F11.imprint","IMPRINT",EDGE,{"disambiguationData":[TD([[subQ14,-1.0]])],"derivedFrom":subQ9});var subQ16=makeQuery(id+"F11.imprint","IMPRINT",EDGE,{"disambiguationData":[TD([[makeQuery(id+"F11.imprint","INTERSECT",VERTEX,{"derivedFrom":[sQuery(id+"F11.wireOp",EDGE,"E4.bottom"),subQ9]}),-1.0]])],"derivedFrom":subQ9});Q5=makeQuery(id+"F13.opFillet","BLEND_EDGE",EDGE,{"blendedFrom":[makeQuery(id+"F12.boolean.opBoolean","COPY",EDGE,{"derivedFrom":makeQuery(id+"F12.opExtrude","CAP_EDGE",EDGE,{"disambiguationData":[OSD([subQ9]),TDD([subQ16,subQ15,subQ13])],"isStart":false})}),makeQuery(id+"F12.boolean.opBoolean","SPLIT",FACE,{"disambiguationData":[TD([makeQuery(id+"F12.opExtrude","SWEPT_FACE",FACE,{"disambiguationData":[OSD([subQ5]),TDD([makeQuery(id+"F11.imprint","IMPRINT",EDGE,{"disambiguationData":[TD([[subQ10,-1.0]])],"derivedFrom":subQ5}),makeQuery(id+"F11.imprint","IMPRINT",EDGE,{"disambiguationData":[TD([[subQ7,1.0]])],"derivedFrom":subQ5}),makeQuery(id+"F11.imprint","IMPRINT",EDGE,{"disambiguationData":[TD([[makeQuery(id+"F11.imprint","INTERSECT",VERTEX,{"derivedFrom":[subQ5,sQuery(id+"F11.wireOp",EDGE,"E3.right")]}),1.0]])],"derivedFrom":subQ5})])]})])],"derivedFrom":makeQuery(id+"F9.opExtrude","CAP_FACE",FACE,{"disambiguationData":[OSD([subQ1,subQ3,subQ2,subQ0])],"isStart":false})})],"blendedInto":[makeQuery(id+"F12.boolean.opBoolean","SPLIT",FACE,{"disambiguationData":[TD([makeQuery(id+"F12.opExtrude","SWEPT_FACE",FACE,{"disambiguationData":[OSD([subQ5]),TDD([makeQuery(id+"F11.imprint","IMPRINT",EDGE,{"disambiguationData":[TD([[subQ10,-1.0]])],"derivedFrom":subQ5}),makeQuery(id+"F11.imprint","IMPRINT",EDGE,{"disambiguationData":[TD([[subQ7,1.0]])],"derivedFrom":subQ5}),makeQuery(id+"F11.imprint","IMPRINT",EDGE,{"disambiguationData":[TD([[makeQuery(id+"F11.imprint","INTERSECT",VERTEX,{"derivedFrom":[subQ5,sQuery(id+"F11.wireOp",EDGE,"E3.right")]}),1.0]])],"derivedFrom":subQ5})])]})])],"derivedFrom":makeQuery(id+"F9.opExtrude","CAP_FACE",FACE,{"disambiguationData":[OSD([subQ1,subQ3,subQ2,subQ0])],"isStart":false})})]});}
            var Q6;
            {var subQ0=sQuery(id+"F0.wireOp",EDGE,"E0.right");var subQ1=sQuery(id+"F0.wireOp",EDGE,"E0.left");var subQ2=sQuery(id+"F0.wireOp",EDGE,"E0.top");var subQ3=sQuery(id+"F0.wireOp",EDGE,"E0.bottom");var subQ5=sQuery(id+"F11.wireOp",EDGE,"E4.left");var subQ6=sQuery(id+"F11.wireOp",EDGE,"E3.bottom");var subQ7=makeQuery(id+"F11.imprint","INTERSECT",VERTEX,{"derivedFrom":[subQ6,subQ5]});var subQ8=makeQuery(id+"F9.opExtrude","CAP_EDGE",EDGE,{"disambiguationData":[OSD([subQ3])],"isStart":false});var subQ10=makeQuery(id+"F11.imprint","IMPRINT",EDGE,{"disambiguationData":[TD([[subQ7,1.0]])],"derivedFrom":subQ5});var subQ11=makeQuery(id+"F11.imprint","INTERSECT",VERTEX,{"derivedFrom":[subQ8,subQ5]});var subQ12=makeQuery(id+"F11.imprint","IMPRINT",EDGE,{"disambiguationData":[TD([[subQ11,-1.0]])],"derivedFrom":subQ5});var subQ13=makeQuery(id+"F11.imprint","IMPRINT",EDGE,{"disambiguationData":[TD([[makeQuery(id+"F11.imprint","INTERSECT",VERTEX,{"derivedFrom":[sQuery(id+"F11.wireOp",EDGE,"E4.bottom"),subQ5]}),-1.0]])],"derivedFrom":subQ5});var subQ14=makeQuery(id+"F9.opExtrude","CAP_EDGE",EDGE,{"disambiguationData":[OSD([subQ1])],"isStart":false});var subQ16=makeQuery(id+"F11.imprint","INTERSECT",VERTEX,{"derivedFrom":[subQ14,subQ6]});Q6=makeQuery(id+"F13.opFillet","BLEND_EDGE",EDGE,{"blendedFrom":[makeQuery(id+"F12.boolean.opBoolean","COPY",EDGE,{"derivedFrom":makeQuery(id+"F12.opExtrude","CAP_EDGE",EDGE,{"disambiguationData":[OSD([subQ5]),TDD([subQ13,subQ12,subQ10])],"isStart":false})}),makeQuery(id+"F12.boolean.opBoolean","SPLIT",FACE,{"disambiguationData":[TD([makeQuery(id+"F12.opExtrude","SWEPT_FACE",FACE,{"disambiguationData":[OSD([subQ6]),TDD([makeQuery(id+"F11.imprint","IMPRINT",EDGE,{"disambiguationData":[TD([[makeQuery(id+"F11.imprint","INTERSECT",VERTEX,{"derivedFrom":[subQ6,sQuery(id+"F11.wireOp",EDGE,"E3.left")]}),-1.0]])],"derivedFrom":subQ6}),makeQuery(id+"F11.imprint","IMPRINT",EDGE,{"disambiguationData":[TD([[subQ16,-1.0]])],"derivedFrom":subQ6}),makeQuery(id+"F11.imprint","IMPRINT",EDGE,{"disambiguationData":[TD([[subQ7,1.0]])],"derivedFrom":subQ6})])]})])],"derivedFrom":makeQuery(id+"F9.opExtrude","CAP_FACE",FACE,{"disambiguationData":[OSD([subQ3,subQ2,subQ1,subQ0])],"isStart":false})})],"blendedInto":[makeQuery(id+"F12.boolean.opBoolean","SPLIT",FACE,{"disambiguationData":[TD([makeQuery(id+"F12.opExtrude","SWEPT_FACE",FACE,{"disambiguationData":[OSD([subQ6]),TDD([makeQuery(id+"F11.imprint","IMPRINT",EDGE,{"disambiguationData":[TD([[makeQuery(id+"F11.imprint","INTERSECT",VERTEX,{"derivedFrom":[subQ6,sQuery(id+"F11.wireOp",EDGE,"E3.left")]}),-1.0]])],"derivedFrom":subQ6}),makeQuery(id+"F11.imprint","IMPRINT",EDGE,{"disambiguationData":[TD([[subQ16,-1.0]])],"derivedFrom":subQ6}),makeQuery(id+"F11.imprint","IMPRINT",EDGE,{"disambiguationData":[TD([[subQ7,1.0]])],"derivedFrom":subQ6})])]})])],"derivedFrom":makeQuery(id+"F9.opExtrude","CAP_FACE",FACE,{"disambiguationData":[OSD([subQ3,subQ2,subQ1,subQ0])],"isStart":false})})]});}
            var Q7;
            {var subQ0=sQuery(id+"F0.wireOp",EDGE,"E0.right");var subQ1=sQuery(id+"F0.wireOp",EDGE,"E0.left");var subQ2=sQuery(id+"F0.wireOp",EDGE,"E0.top");var subQ3=sQuery(id+"F0.wireOp",EDGE,"E0.bottom");var subQ5=sQuery(id+"F11.wireOp",EDGE,"E4.left");var subQ6=sQuery(id+"F11.wireOp",EDGE,"E3.bottom");var subQ7=makeQuery(id+"F11.imprint","INTERSECT",VERTEX,{"derivedFrom":[subQ6,subQ5]});var subQ11=makeQuery(id+"F9.opExtrude","CAP_EDGE",EDGE,{"disambiguationData":[OSD([subQ1])],"isStart":false});var subQ13=makeQuery(id+"F11.imprint","IMPRINT",EDGE,{"disambiguationData":[TD([[subQ7,1.0]])],"derivedFrom":subQ6});var subQ14=makeQuery(id+"F11.imprint","INTERSECT",VERTEX,{"derivedFrom":[subQ11,subQ6]});var subQ15=makeQuery(id+"F11.imprint","IMPRINT",EDGE,{"disambiguationData":[TD([[subQ14,-1.0]])],"derivedFrom":subQ6});var subQ16=makeQuery(id+"F11.imprint","IMPRINT",EDGE,{"disambiguationData":[TD([[makeQuery(id+"F11.imprint","INTERSECT",VERTEX,{"derivedFrom":[subQ6,sQuery(id+"F11.wireOp",EDGE,"E3.left")]}),-1.0]])],"derivedFrom":subQ6});Q7=makeQuery(id+"F13.opFillet","BLEND_EDGE",EDGE,{"blendedFrom":[makeQuery(id+"F12.boolean.opBoolean","COPY",EDGE,{"derivedFrom":makeQuery(id+"F12.opExtrude","CAP_EDGE",EDGE,{"disambiguationData":[OSD([subQ6]),TDD([subQ16,subQ15,subQ13])],"isStart":false})}),makeQuery(id+"F12.boolean.opBoolean","SPLIT",FACE,{"disambiguationData":[TD([makeQuery(id+"F12.opExtrude","SWEPT_FACE",FACE,{"disambiguationData":[OSD([subQ6]),TDD([subQ16,subQ15,subQ13])]})])],"derivedFrom":makeQuery(id+"F9.opExtrude","CAP_FACE",FACE,{"disambiguationData":[OSD([subQ3,subQ2,subQ1,subQ0])],"isStart":false})})],"blendedInto":[makeQuery(id+"F12.boolean.opBoolean","SPLIT",FACE,{"disambiguationData":[TD([makeQuery(id+"F12.opExtrude","SWEPT_FACE",FACE,{"disambiguationData":[OSD([subQ6]),TDD([subQ16,subQ15,subQ13])]})])],"derivedFrom":makeQuery(id+"F9.opExtrude","CAP_FACE",FACE,{"disambiguationData":[OSD([subQ3,subQ2,subQ1,subQ0])],"isStart":false})})]});}
            fillet(context, id + "F14", {"entities" : qUnion([Q0, Q1, Q2, Q3, Q4, Q5, Q6, Q7]), "radius" : 6.35 * mm, "tangentPropagation" : true, "allowEdgeOverflow" : false});
        }
        {
            var Q0;
            Q0=makeQuery(id+"F1.opExtrude","CAP_FACE",FACE,{"disambiguationData":[OSD([sQuery(id+"F0.wireOp",EDGE,"E0.bottom"),sQuery(id+"F0.wireOp",EDGE,"E0.top"),sQuery(id+"F0.wireOp",EDGE,"E0.left"),sQuery(id+"F0.wireOp",EDGE,"E0.right")])],"isStart":true});
            var sketch = newSketch(context, id + "F15", { "sketchPlane" : qUnion([Q0])});
            skLineSegment(sketch, "E5.0", {"start": v(-68.58, 89.53) * mm, "end": v(68.58, 89.53) * mm});
            skArc(sketch, "E5.1", {"start": v(89.54, 68.58) * mm, "mid": v(83.4, 83.4) * mm, "end": v(68.58, 89.53) * mm});
            skArc(sketch, "E5.2", {"start": v(-68.58, 89.53) * mm, "mid": v(-83.4, 83.4) * mm, "end": v(-89.54, 68.58) * mm});
            skLineSegment(sketch, "E5.3", {"start": v(89.54, 68.58) * mm, "end": v(89.54, -68.58) * mm});
            skLineSegment(sketch, "E5.4", {"start": v(-89.54, 68.58) * mm, "end": v(-89.54, -68.58) * mm});
            skArc(sketch, "E5.5", {"start": v(-89.54, -68.58) * mm, "mid": v(-83.4, -83.4) * mm, "end": v(-68.58, -89.53) * mm});
            skLineSegment(sketch, "E5.6", {"start": v(-68.58, -89.53) * mm, "end": v(68.58, -89.53) * mm});
            skArc(sketch, "E5.7", {"start": v(68.58, -89.53) * mm, "mid": v(83.4, -83.4) * mm, "end": v(89.53, -68.58) * mm});
            skArc(sketch, "E6.0", {"start": v(95.89, 68.58) * mm, "mid": v(87.89, 87.89) * mm, "end": v(68.58, 95.89) * mm});
            skLineSegment(sketch, "E6.1", {"start": v(95.89, -68.58) * mm, "end": v(95.89, 68.58) * mm});
            skLineSegment(sketch, "E6.2", {"start": v(68.58, 95.89) * mm, "end": v(-68.58, 95.89) * mm});
            skArc(sketch, "E6.3", {"start": v(68.58, -95.89) * mm, "mid": v(87.89, -87.89) * mm, "end": v(95.89, -68.58) * mm});
            skArc(sketch, "E6.4", {"start": v(-68.58, 95.89) * mm, "mid": v(-87.89, 87.89) * mm, "end": v(-95.89, 68.58) * mm});
            skLineSegment(sketch, "E6.5", {"start": v(-95.89, 68.58) * mm, "end": v(-95.89, -68.58) * mm});
            skArc(sketch, "E6.6", {"start": v(-95.89, -68.58) * mm, "mid": v(-87.89, -87.89) * mm, "end": v(-68.58, -95.89) * mm});
            skLineSegment(sketch, "E6.7", {"start": v(-68.58, -95.89) * mm, "end": v(68.58, -95.89) * mm});
            skSolve(sketch);
        }
        {
            var Q0;
            Q0=makeQuery(id+"F15.imprint","IMPRINT",FACE,{"disambiguationData":[TD([[makeQuery(id+"F15.imprint","IMPRINT",EDGE,{"derivedFrom":sQuery(id+"F15.wireOp",EDGE,"E5.0")}),-1.0]])]});
            extrude(context, id + "F16", {"entities" : qUnion([Q0]), "operationType" : NewBodyOperationType.REMOVE, "oppositeDirection" : true, "depth" : 25.4 * mm});
        }
        {
            var Q0;
            {var subQ0=sQuery(id+"F0.wireOp",EDGE,"E0.left");Q0=makeQuery(id+"F3.opShell","OFFSET_EDGE",EDGE,{"disambiguationData":[OSD([subQ0]),TDD([makeQuery(id+"F1.opExtrude","CAP_EDGE",EDGE,{"disambiguationData":[OSD([subQ0])],"isStart":true})])]});}
            fillet(context, id + "F17", {"entities" : qUnion([Q0]), "radius" : 7.62 * mm, "tangentPropagation" : true, "allowEdgeOverflow" : false});
        }
        {
            var Q0;
            Q0=makeQuery(id+"F6.boolean.opBoolean","COPY",EDGE,{"derivedFrom":makeQuery(id+"F6.opExtrude","CAP_EDGE",EDGE,{"disambiguationData":[OSD([sQuery(id+"F4.wireOp",EDGE,"E1.left")])],"isStart":true})});
            var Q1;
            Q1=makeQuery(id+"F6.boolean.opBoolean","INTERSECT",EDGE,{"derivedFrom":[makeQuery(id+"F3.opShell","OFFSET_FACE",FACE,{"disambiguationData":[OSD([sQuery(id+"F0.wireOp",EDGE,"E0.bottom")])]}),makeQuery(id+"F6.opExtrude","SWEPT_FACE",FACE,{"disambiguationData":[OSD([sQuery(id+"F4.wireOp",EDGE,"E1.left")])]})]});
            var Q2;
            Q2=makeQuery(id+"F7.boolean.opBoolean","INTERSECT",EDGE,{"derivedFrom":[makeQuery(id+"F3.opShell","OFFSET_FACE",FACE,{"disambiguationData":[OSD([sQuery(id+"F0.wireOp",EDGE,"E0.right")])]}),makeQuery(id+"F7.opExtrude","SWEPT_FACE",FACE,{"disambiguationData":[OSD([sQuery(id+"F5.wireOp",EDGE,"E2.left")])]})]});
            var Q3;
            Q3=makeQuery(id+"F7.boolean.opBoolean","COPY",EDGE,{"derivedFrom":makeQuery(id+"F7.opExtrude","CAP_EDGE",EDGE,{"disambiguationData":[OSD([sQuery(id+"F5.wireOp",EDGE,"E2.left")])],"isStart":true})});
            var Q4;
            Q4=makeQuery(id+"F7.boolean.opBoolean","INTERSECT",EDGE,{"derivedFrom":[makeQuery(id+"F1.opExtrude","SWEPT_FACE",FACE,{"disambiguationData":[OSD([sQuery(id+"F0.wireOp",EDGE,"E0.left")])]}),makeQuery(id+"F7.opExtrude","SWEPT_FACE",FACE,{"disambiguationData":[OSD([sQuery(id+"F5.wireOp",EDGE,"E2.right")])]})]});
            var Q5;
            Q5=makeQuery(id+"F7.boolean.opBoolean","INTERSECT",EDGE,{"derivedFrom":[makeQuery(id+"F3.opShell","OFFSET_FACE",FACE,{"disambiguationData":[OSD([sQuery(id+"F0.wireOp",EDGE,"E0.left")])]}),makeQuery(id+"F7.opExtrude","SWEPT_FACE",FACE,{"disambiguationData":[OSD([sQuery(id+"F5.wireOp",EDGE,"E2.right")])]})]});
            var Q6;
            Q6=makeQuery(id+"F6.boolean.opBoolean","INTERSECT",EDGE,{"derivedFrom":[makeQuery(id+"F1.opExtrude","SWEPT_FACE",FACE,{"disambiguationData":[OSD([sQuery(id+"F0.wireOp",EDGE,"E0.top")])]}),makeQuery(id+"F6.opExtrude","SWEPT_FACE",FACE,{"disambiguationData":[OSD([sQuery(id+"F4.wireOp",EDGE,"E1.right")])]})]});
            var Q7;
            Q7=makeQuery(id+"F6.boolean.opBoolean","INTERSECT",EDGE,{"derivedFrom":[makeQuery(id+"F3.opShell","OFFSET_FACE",FACE,{"disambiguationData":[OSD([sQuery(id+"F0.wireOp",EDGE,"E0.top")])]}),makeQuery(id+"F6.opExtrude","SWEPT_FACE",FACE,{"disambiguationData":[OSD([sQuery(id+"F4.wireOp",EDGE,"E1.right")])]})]});
            var Q8;
            Q8=makeQuery(id+"F16.boolean.opBoolean","COPY",EDGE,{"derivedFrom":makeQuery(id+"F16.opExtrude","CAP_EDGE",EDGE,{"disambiguationData":[OSD([sQuery(id+"F15.wireOp",EDGE,"E5.0")])],"isStart":true})});
            var Q9;
            Q9=makeQuery(id+"F16.boolean.opBoolean","INTERSECT",EDGE,{"derivedFrom":[makeQuery(id+"F3.opShell","OFFSET_FACE",FACE,{"disambiguationData":[OSD([sQuery(id+"F0.wireOp",EDGE,"E0.bottom"),sQuery(id+"F0.wireOp",EDGE,"E0.top"),sQuery(id+"F0.wireOp",EDGE,"E0.left"),sQuery(id+"F0.wireOp",EDGE,"E0.right")])]}),makeQuery(id+"F16.opExtrude","SWEPT_FACE",FACE,{"disambiguationData":[OSD([sQuery(id+"F15.wireOp",EDGE,"E5.0")])]})]});
            var Q10;
            {var subQ0=sQuery(id+"F0.wireOp",EDGE,"E0.right");var subQ1=sQuery(id+"F0.wireOp",EDGE,"E0.left");var subQ2=sQuery(id+"F0.wireOp",EDGE,"E0.top");var subQ3=sQuery(id+"F0.wireOp",EDGE,"E0.bottom");Q10=makeQuery(id+"F9.opExtrude","CAP_EDGE",EDGE,{"disambiguationData":[OSD([subQ3,subQ2,subQ1,subQ0]),TDD([makeQuery(id+"F2.opFillet","BLEND_EDGE",EDGE,{"blendedFrom":[makeQuery(id+"F1.opExtrude","SWEPT_EDGE",EDGE,{"disambiguationData":[OSD([subQ2,subQ0])]}),makeQuery(id+"F1.opExtrude","CAP_FACE",FACE,{"disambiguationData":[OSD([subQ3,subQ2,subQ1,subQ0])],"isStart":true})],"blendedInto":[makeQuery(id+"F1.opExtrude","CAP_FACE",FACE,{"disambiguationData":[OSD([subQ3,subQ2,subQ1,subQ0])],"isStart":true})]})])],"isStart":false});}
            var Q11;
            {var subQ0=sQuery(id+"F0.wireOp",EDGE,"E0.right");var subQ1=sQuery(id+"F0.wireOp",EDGE,"E0.left");var subQ2=sQuery(id+"F0.wireOp",EDGE,"E0.top");var subQ3=sQuery(id+"F0.wireOp",EDGE,"E0.bottom");Q11=makeQuery(id+"F10.opShell","OFFSET_EDGE",EDGE,{"disambiguationData":[OSD([subQ3,subQ2,subQ1,subQ0]),TDD([makeQuery(id+"F9.opExtrude","CAP_EDGE",EDGE,{"disambiguationData":[OSD([subQ3,subQ2,subQ1,subQ0]),TDD([makeQuery(id+"F2.opFillet","BLEND_EDGE",EDGE,{"blendedFrom":[makeQuery(id+"F1.opExtrude","SWEPT_EDGE",EDGE,{"disambiguationData":[OSD([subQ2,subQ0])]}),makeQuery(id+"F1.opExtrude","CAP_FACE",FACE,{"disambiguationData":[OSD([subQ3,subQ2,subQ1,subQ0])],"isStart":true})],"blendedInto":[makeQuery(id+"F1.opExtrude","CAP_FACE",FACE,{"disambiguationData":[OSD([subQ3,subQ2,subQ1,subQ0])],"isStart":true})]})])],"isStart":false})])]});}
            fillet(context, id + "F18", {"entities" : qUnion([Q0, Q1, Q2, Q3, Q4, Q5, Q6, Q7, Q8, Q9, Q10, Q11]), "radius" : 1.27 * mm, "tangentPropagation" : true, "allowEdgeOverflow" : false});
        }
    });
